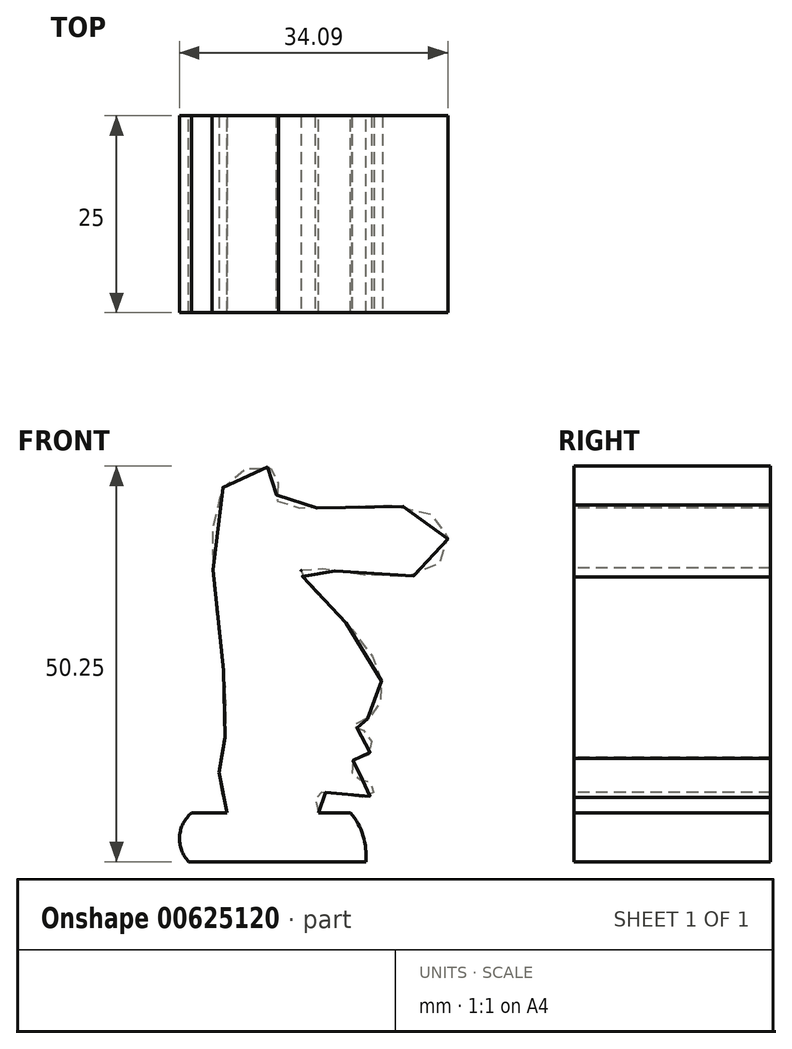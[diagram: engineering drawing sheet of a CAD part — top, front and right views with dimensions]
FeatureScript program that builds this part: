
annotation { "Feature Type Name" : "Feature", "Feature Type Description" : "" }
export const myFeature = defineFeature(function(context is Context, id is Id, definition is map)
    precondition{}
    {
        {
            var Q0;
            Q0=qCreatedBy(makeId("Front.planeOp"),FACE);
            var sketch = newSketch(context, id + "F0", { "sketchPlane" : qUnion([Q0])});
            skLineSegment(sketch, "E0", {"start": v(-18.52, -23.18) * mm, "end": v(3.98, -23.18) * mm});
            skLineSegment(sketch, "E1", {"start": v(-18.14, -16.97) * mm, "end": v(2.04, -16.97) * mm});
            skArc(sketch, "E2", {"start": v(3.98, -23.18) * mm, "mid": v(3.62, -19.88) * mm, "end": v(2.04, -16.97) * mm});
            skArc(sketch, "E3", {"start": v(-18.14, -16.97) * mm, "mid": v(-19.68, -20) * mm, "end": v(-18.52, -23.18) * mm});
            skFitSpline(sketch, "E4", {"points": [v(-13.67, -16.97) * mm, v(-14.64, -10.96) * mm, v(-13.67, -4.17) * mm, v(-13.67, 25.12) * mm, v(-7.27, 26.09) * mm, v(-7.08, 22.4) * mm, v(12.51, 20.85) * mm, v(11.93, 13.67) * mm, v(-4.17, 13.87) * mm, v(4.75, 3) * mm, v(4.56, -4.75) * mm, v(2.23, -5.92) * mm, v(4.36, -7.08) * mm, v(3.98, -9.99) * mm, v(2.62, -9.99) * mm, v(2.42, -12.32) * mm, v(4.56, -13.1) * mm, v(4.56, -14.84) * mm, v(-2.04, -14.45) * mm, v(-2.04, -16.97) * mm], "startDerivative": vector(-31.33, 122.75) * mm, "endDerivative": vector(33.28, -98.68) * mm});
            skSolve(sketch);
        }
        {
            var Q0;
            {var subQ0=sQuery(id+"F0.wireOp",EDGE,"E4");Q0=makeQuery(id+"F0.imprint","IMPRINT",FACE,{"disambiguationData":[TD([[makeQuery(id+"F0.imprint","IMPRINT",EDGE,{"derivedFrom":subQ0}),-1.0]])]});}
            var Q1;
            Q1=makeQuery(id+"F0.imprint","IMPRINT",FACE,{"disambiguationData":[TD([[makeQuery(id+"F0.imprint","IMPRINT",EDGE,{"derivedFrom":sQuery(id+"F0.wireOp",EDGE,"E0")}),1.0]])]});
            extrude(context, id + "F1", {"entities" : qUnion([Q0, Q1]), "depth" : 25 * mm, "offsetDistance" : 25 * mm});
        }
    });
